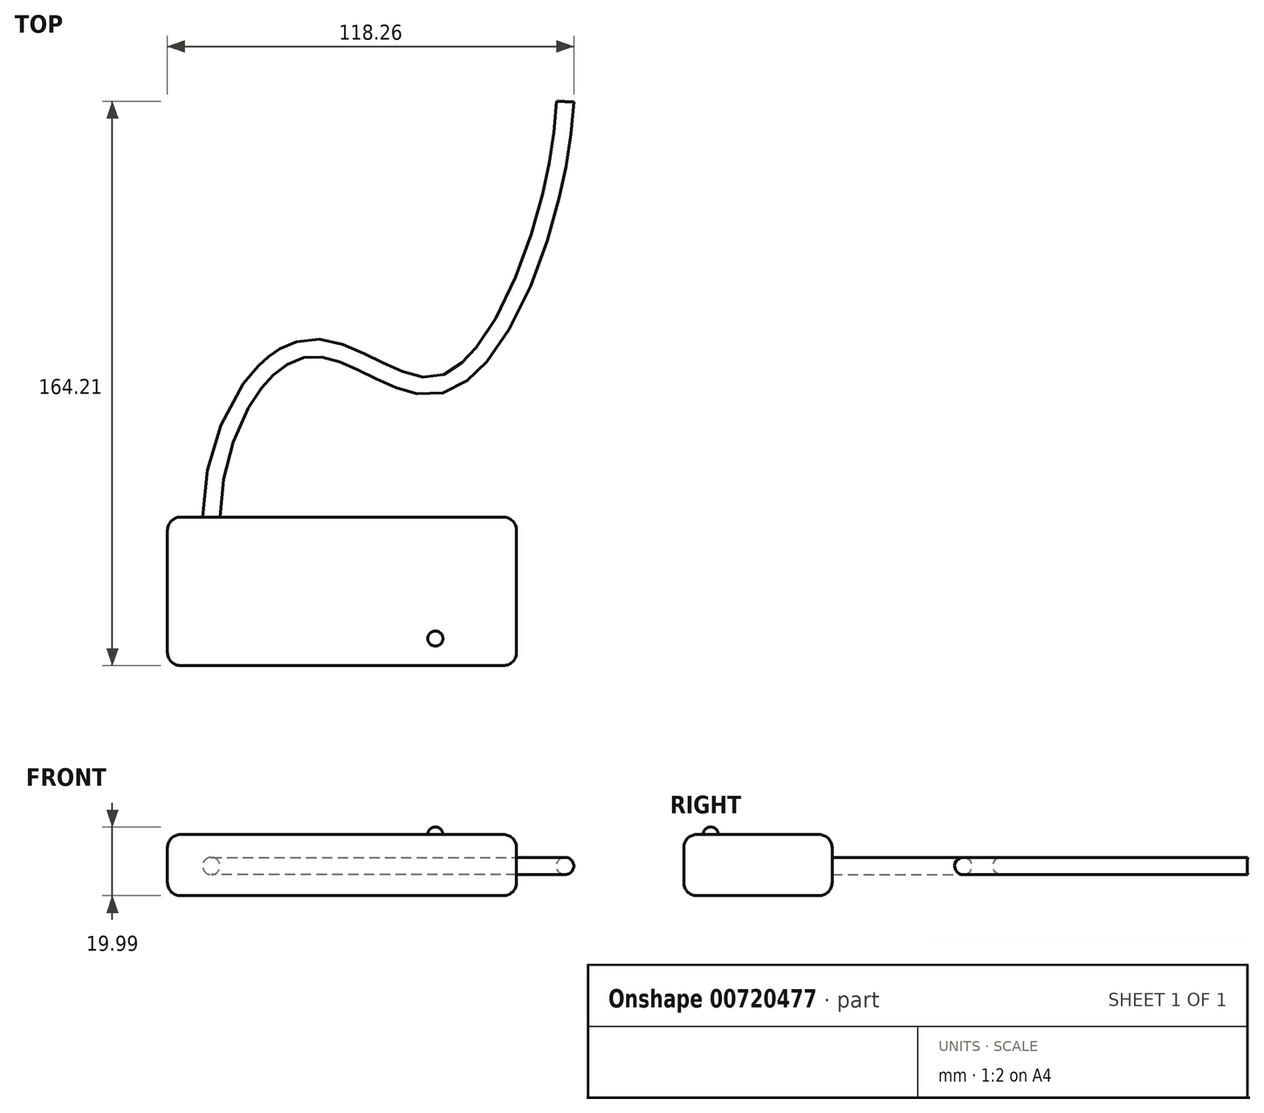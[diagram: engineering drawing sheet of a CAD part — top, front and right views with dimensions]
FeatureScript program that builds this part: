
annotation { "Feature Type Name" : "Feature", "Feature Type Description" : "" }
export const myFeature = defineFeature(function(context is Context, id is Id, definition is map)
    precondition{}
    {
        {
            var Q0;
            Q0=qCreatedBy(makeId("Top.planeOp"),FACE);
            var sketch = newSketch(context, id + "F0", { "sketchPlane" : qUnion([Q0])});
            skLineSegment(sketch, "E0.bottom", {"start": v(0, 0) * mm, "end": v(101.6, 0) * mm});
            skLineSegment(sketch, "E0.top", {"start": v(0, 43.18) * mm, "end": v(101.6, 43.18) * mm});
            skLineSegment(sketch, "E0.left", {"start": v(0, 0) * mm, "end": v(0, 43.18) * mm});
            skLineSegment(sketch, "E0.right", {"start": v(101.6, 0) * mm, "end": v(101.6, 43.18) * mm});
            skSolve(sketch);
        }
        {
            var Q0;
            Q0 = qSketchRegion(id + "F0", true);
            extrude(context, id + "F1", {"entities" : qUnion([Q0]), "depth" : 17.78 * mm, "offsetDistance" : 25.4 * mm});
        }
        {
            var Q0;
            Q0=makeQuery(id+"F1.opExtrude","SWEPT_EDGE",EDGE,{"disambiguationData":[OSD([sQuery(id+"F0.wireOp",EDGE,"E0.bottom"),sQuery(id+"F0.wireOp",EDGE,"E0.left")])]});
            var Q1;
            Q1=makeQuery(id+"F1.opExtrude","CAP_EDGE",EDGE,{"disambiguationData":[OSD([sQuery(id+"F0.wireOp",EDGE,"E0.bottom")])],"isStart":false});
            var Q2;
            Q2=makeQuery(id+"F1.opExtrude","CAP_EDGE",EDGE,{"disambiguationData":[OSD([sQuery(id+"F0.wireOp",EDGE,"E0.left")])],"isStart":false});
            var Q3;
            Q3=makeQuery(id+"F1.opExtrude","CAP_EDGE",EDGE,{"disambiguationData":[OSD([sQuery(id+"F0.wireOp",EDGE,"E0.left")])],"isStart":true});
            var Q4;
            Q4=makeQuery(id+"F1.opExtrude","CAP_EDGE",EDGE,{"disambiguationData":[OSD([sQuery(id+"F0.wireOp",EDGE,"E0.bottom")])],"isStart":true});
            var Q5;
            Q5=makeQuery(id+"F1.opExtrude","SWEPT_EDGE",EDGE,{"disambiguationData":[OSD([sQuery(id+"F0.wireOp",EDGE,"E0.top"),sQuery(id+"F0.wireOp",EDGE,"E0.left")])]});
            var Q6;
            Q6=makeQuery(id+"F1.opExtrude","SWEPT_EDGE",EDGE,{"disambiguationData":[OSD([sQuery(id+"F0.wireOp",EDGE,"E0.bottom"),sQuery(id+"F0.wireOp",EDGE,"E0.right")])]});
            var Q7;
            Q7=makeQuery(id+"F1.opExtrude","CAP_EDGE",EDGE,{"disambiguationData":[OSD([sQuery(id+"F0.wireOp",EDGE,"E0.top")])],"isStart":false});
            var Q8;
            Q8=makeQuery(id+"F1.opExtrude","SWEPT_EDGE",EDGE,{"disambiguationData":[OSD([sQuery(id+"F0.wireOp",EDGE,"E0.top"),sQuery(id+"F0.wireOp",EDGE,"E0.right")])]});
            var Q9;
            Q9=makeQuery(id+"F1.opExtrude","CAP_EDGE",EDGE,{"disambiguationData":[OSD([sQuery(id+"F0.wireOp",EDGE,"E0.top")])],"isStart":true});
            var Q10;
            Q10=makeQuery(id+"F1.opExtrude","CAP_EDGE",EDGE,{"disambiguationData":[OSD([sQuery(id+"F0.wireOp",EDGE,"E0.right")])],"isStart":true});
            var Q11;
            Q11=makeQuery(id+"F1.opExtrude","CAP_EDGE",EDGE,{"disambiguationData":[OSD([sQuery(id+"F0.wireOp",EDGE,"E0.right")])],"isStart":false});
            fillet(context, id + "F2", {"entities" : qUnion([Q0, Q1, Q2, Q3, Q4, Q5, Q6, Q7, Q8, Q9, Q10, Q11]), "radius" : 3.8 * mm, "tangentPropagation" : true, "allowEdgeOverflow" : false});
        }
        {
            var Q0;
            Q0=qCreatedBy(makeId("Right.planeOp"),FACE);
            cPlane(context, id + "F3", {"entities" : qUnion([Q0]), "cplaneType" : CPlaneType.OFFSET, "offset" : 77.98 * mm, "width" : 152.4 * mm, "height" : 152.4 * mm});
        }
        {
            var Q0;
            Q0=qCreatedBy(id+"F3.planeOp",FACE);
            var sketch = newSketch(context, id + "F4", { "sketchPlane" : qUnion([Q0])});
            skLineSegment(sketch, "E1", {"start": v(7.84, 17.78) * mm, "end": v(7.84, 20) * mm});
            skArc(sketch, "E2", {"start": v(10.05, 17.78) * mm, "mid": v(9.4, 19.34) * mm, "end": v(7.84, 20) * mm});
            skLineSegment(sketch, "E3", {"start": v(7.84, 17.78) * mm, "end": v(10.05, 17.78) * mm});
            skSolve(sketch);
        }
        {
            var Q0;
            Q0 = qSketchRegion(id + "F4", true);
            var Q1;
            Q1=sQuery(id+"F4.wireOp",EDGE,"E1");
            revolve(context, id + "F5", {"operationType" : NewBodyOperationType.ADD, "surfaceOperationType" : NewSurfaceOperationType.NEW, "entities" : qUnion([Q0]), "axis" : qUnion([Q1]), "revolveType" : RevolveType.FULL});
        }
        {
            var Q0;
            Q0=qCreatedBy(makeId("Top.planeOp"),FACE);
            cPlane(context, id + "F6", {"entities" : qUnion([Q0]), "cplaneType" : CPlaneType.OFFSET, "offset" : 8.64 * mm, "width" : 152.4 * mm, "height" : 152.4 * mm});
        }
        {
            var Q0;
            Q0=qCreatedBy(id+"F6.planeOp",FACE);
            var sketch = newSketch(context, id + "F7", { "sketchPlane" : qUnion([Q0])});
            skFitSpline(sketch, "E4", {"points": [v(12.77, 43.18) * mm, v(41.87, 92.46) * mm, v(79.79, 81.87) * mm, v(115.74, 164.13) * mm], "startDerivative": vector(3.62, 235.85) * mm, "endDerivative": vector(10.86, 230.37) * mm});
            skSolve(sketch);
        }
        {
            var Q0;
            Q0=makeQuery(id+"F1.opExtrude","SWEPT_FACE",FACE,{"disambiguationData":[OSD([sQuery(id+"F0.wireOp",EDGE,"E0.top")])]});
            var sketch = newSketch(context, id + "F8", { "sketchPlane" : qUnion([Q0])});
            skCircle(sketch, "E5", {"center": v(-12.77, 8.64) * mm, "radius": 2.52 * mm});
            skSolve(sketch);
        }
        {
            var Q0;
            Q0=makeQuery(id+"F8.imprint","IMPRINT",FACE,{"disambiguationData":[TD([[makeQuery(id+"F8.imprint","IMPRINT",EDGE,{"derivedFrom":sQuery(id+"F8.wireOp",EDGE,"E5")}),1.0]])]});
            var Q1;
            Q1=sQuery(id+"F7.wireOp",EDGE,"E4");
            sweep(context, id + "F9", {"operationType" : NewBodyOperationType.ADD, "profiles" : qUnion([Q0]), "path" : qUnion([Q1])});
        }
    });
